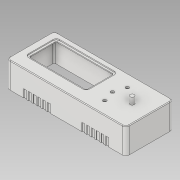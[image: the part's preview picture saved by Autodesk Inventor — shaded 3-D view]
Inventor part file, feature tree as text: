
AUTODESK INVENTOR PART (.ipt)
format: ipt  version: 2019 (Build 230136000, 136)  size: 326,144 bytes
history: native  units: mm
features: sketch x10, extrude x9, projected_geometry x5, fillet x4, pattern_linear x2, other x1, hole x1, mirror x1
ambient origin geometry x8: Origin, YZ Plane, XZ Plane, XY Plane, X Axis, Y Axis, Z Axis, Center Point
bodies: Body1 (feature_tree)
feature tree (33):
  other  "Sólido1"
  extrude  "Extrusión1"  Depth=70.0mm
  fillet  "Empalme1"  Radius=2.8mm
  extrude  "Extrusión2"  Depth=2.8mm
  extrude  "Extrusión8"  Depth=5.0mm
  fillet  "Empalme3"  Radius=3.3mm
  hole  "Agujero2"  [1 undecoded]
  fillet  "Empalme4"  Radius=90.0mm
  extrude  "Extrusión10"  Depth=55.0mm
  fillet  "Empalme6"  Radius=16.0mm
  extrude  "Extrusión11"  Depth=5.0mm
  extrude  "Extrusión12"  Depth=1.5mm TaperAngle=0.0deg
  extrude  "Extrusión13"  Depth=4.268mm
  pattern_linear  "Patrón rectangular1"  Count1=6 Spacing1=7.0mm
  pattern_linear  "Patrón rectangular2"  Count1=6 Spacing1=7.0mm
  mirror  "Simetría1"
  extrude  "Extrusión14"  Depth=6.0mm
  extrude  "Extrusión15"  Depth=1.0mm
  sketch  "Boceto1"  dims[d0=175.0mm d1=70.0mm d2=2.8mm d3=0.0mm]
  sketch  "Boceto2"  dims[d4=5.0mm d5=2.8mm]
  projected_geometry  "Contorno proyectado1"
  sketch  "Boceto8"  dims[d6=35.0mm d7=0.0mm d40=5.0mm d41=3.3mm d42=0.0mm]
  sketch  "Boceto11"  dims[d43=0.5mm]
  sketch  "Boceto14"  dims[d51=1.8mm d52=6.0mm d53=2.5mm d54=6.0mm d55=90.0deg d56=5.0mm d57=20.594885mm d66=1.0mm d69=90.0mm]
  sketch  "Boceto15"  dims[d70=46.0mm d71=55.0mm d72=16.0mm]
  projected_geometry  "Contorno proyectado18"
  sketch  "Boceto16"  dims[d73=1.5mm d74=0.0mm d75=5.0mm]
  projected_geometry  "Contorno proyectado19"
  sketch  "Boceto17"  dims[d76=2.8mm d77=1.5mm d78=0.0mm]
  projected_geometry  "Contorno proyectado20"
  sketch  "Boceto18"  dims[d80=1.0mm d81=0.0mm d83=4.268mm]
  sketch  "Boceto19"  dims[d84=1.0mm d85=0.0mm d86=60.0mm d88=7.0mm d89=60.0mm d91=7.0mm d92=6.0mm d93=20.0mm d95=6.108652mm d97=5.0mm d98=5.0mm d99=5.0mm d100=5.0mm d101=0.0mm d102=10.0mm d103=0.0mm d44=1.0mm d45=1.0mm d46=1.0mm d47=0.15mm d48=0.25mm d49=0.375mm d50=14.3117mm]
  projected_geometry  "Contorno proyectado21"
note: 1 required parameter value undecoded (feature->parameter linkage not recoverable at this tier; creation-order binding heuristic only, values carry confidence <= 0.55)
